# Revit family: Lighting-UrbanSystem-GEWISS-URBAN[O3]-LED-SIDE_COUPLING_OPTIC_CYCLE-PEDESTRIAN
name_source: partatom
category: Apparecchi per illuminazione
units: mm (PartAtom-declared; Revit-internal decimal feet)

## family parameters
Condiviso = No
Host = Superficie
Numero OmniClass = 23.80.70.00
Punto di calcolo locali = Sì
Quota connettore circolare = Usa diametro
Sorgente d'illuminazione = No
Taglio con vuoti quando caricato = No
Tipo di parte = Normale
Titolo OmniClass = Lighting

## types (4) — shared parameters
Application = External
Catalogue = LIGHTING
Catalogue Range = URBAN [O3]
Colour = Graphite grey
Colour temperature = 4000 K (CRI 70)
Colour temperature: = 4000 K (CRI 70)
Driver type = Constant Current Driver Led
Electrocod = 244C
Finitura = GEWISS - GRIGIO GRAFITE
IDF = dc177271-3986-48b2-bbc2-0ed583cb7899
IDT = e1528f34-313b-4522-a6c0-c97009e176a5
IP degree = IP66
Immagine tipo = GWS7201.jpg
Insulation class = II
LED Life time (L80B10) = 100000H
LED Life time (L90B20) = 50000H
LED LifeTime (L80B20) = 50000H
LED current = 530mA
Maximum surface exposed to the wind = 0,25M2
Minimum distance from the illuminated object = 1M
Operating temperature: = -25 +35 °C
Optic = Cycle and pedestrian - ULOR: 0%
Photobiologic Risk = RG1/RG2 @ 20cm
Pilot current = 530mA
Produttore = GEWISS S.p.A.
Prospetto di default = 1219 mm
R = 160 mm  [stored 0.524934 ft]
R1 = 285 mm  [stored 0.935039 ft]
Risk photobiological = RG1/RG2 @ 20cm
SEO = Street lighting
Shock resistance = IK08 BODY - IK06 LENS
Suitable for = Commercial side brackets with side connection
Suitable for: = Commercial side brackets with side connection
Technical sheet = https://www.gewiss.com
Type of lamp: = LED
Type of light source = LED
URL = https://www.gewiss.com
Version file RFA = 20.11
Vetro = GEWISS - VETRO
Voltage: = 220/240 V - 50/60 Hz
Warranty = 5 years
Working temperature = -25 +35 °C

## per-type parameters (varying)
| type | Descrizione | EAN code | Lumen output (lm) | Modello | No. Chorus modules | Nominal flux (lm) | Number of modules | Power supply operation | System power | Voltage | Weight (kg) | Weight (kg): |
| GWS7208 - URBAN LED 4M 4000K CYC. SIDE B. GRA.GR. | URBAN LED 4M 4000K CYC. SIDE B. GRA.GR. | 8011564802650 | 10560 | GWS7208 | 4 (4x16 LED) | 13400 | 4 (4x16 LED) |  | 105W | 220/240 V - 50/60 Hz - Stand alone and/or possibility of dimmer 1-10 V | 11 | 11 |
| GWS7227 - URBAN LED 3M 4000K BI.CYC.SIDE B.GRA.GR. | URBAN LED 3M 4000K BI.CYC.SIDE B.GRA.GR. | 8011564802766 | 8060 | GWS7227 | 3 (3x16 LED) | 10230 | 3 (3x16 LED) | Bi power | 81W | 220/240 V - 50/60 Hz - Bi-power with self-learning | 10,3 | 10,3 |
| GWS7207 - URBAN LED 3M 4000K CYC. SIDE B. GRA.GR. | URBAN LED 3M 4000K CYC. SIDE B. GRA.GR. | 8011564802643 | 8060 | GWS7207 | 3 (3x16 LED) | 10230 | 3 (3x16 LED) |  | 81W | 220/240 V - 50/60 Hz - Stand alone and/or possibility of dimmer 1-10 V | 10,3 | 10,3 |
| GWS7228 - URBAN LED 4M 4000K BI.CYC.SIDE B.GRA.GR. | URBAN LED 4M 4000K BI.CYC.SIDE B.GRA.GR. | 8011564802773 | 10560 | GWS7228 | 4 (4x16 LED) | 13400 | 4 (4x16 LED) | Bi power | 105W | 220/240 V - 50/60 Hz - Bi-power with self-learning | 11 | 11 |

note: [stored X ft] marks values corroborated as IEEE doubles in the binary element streams (Revit-internal decimal feet)

## geometry (parser evidence)
native form markers: Blend x2
no freeform markers — native parametric forms only
